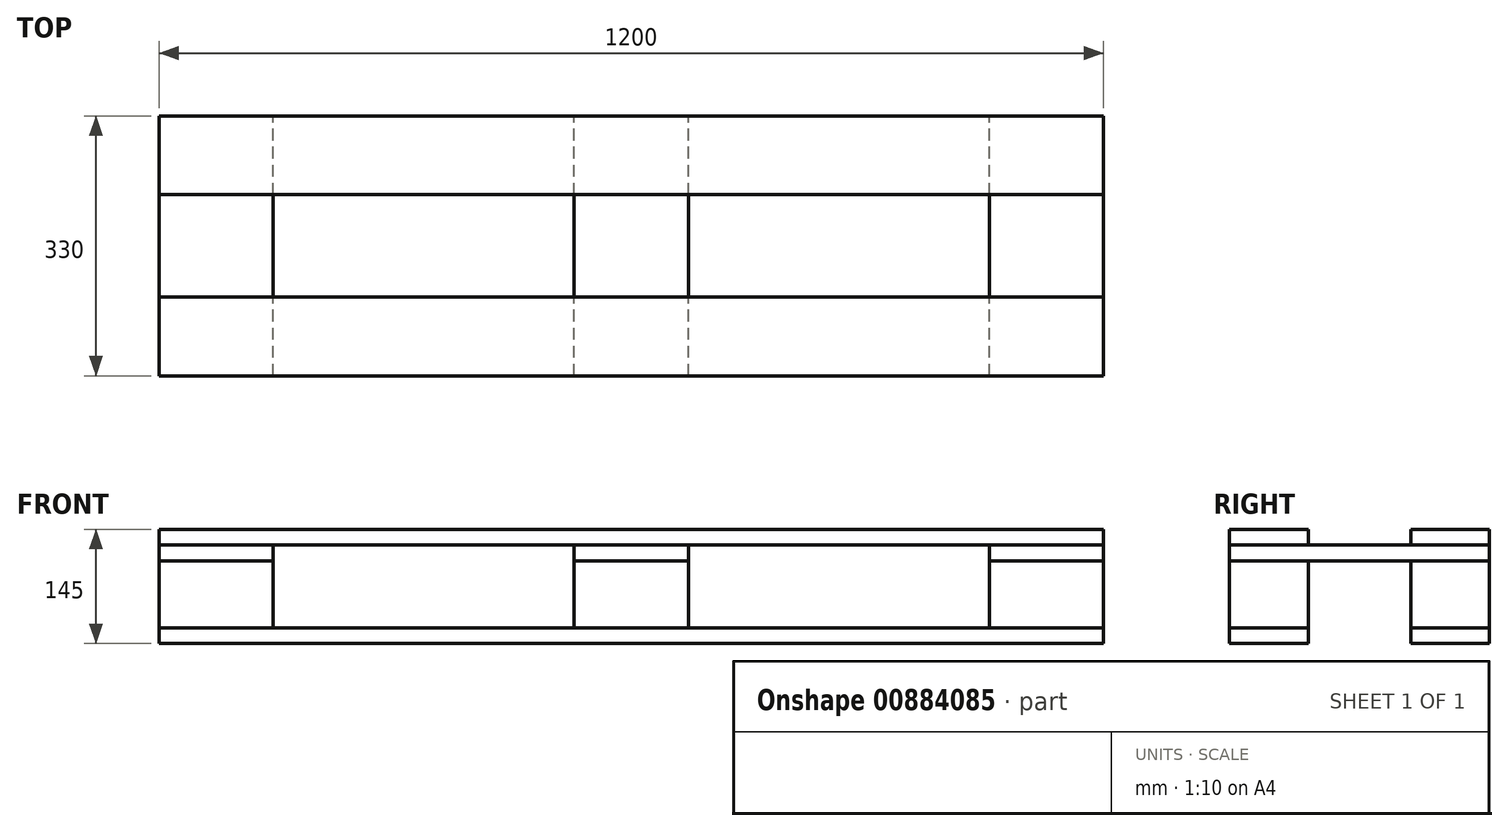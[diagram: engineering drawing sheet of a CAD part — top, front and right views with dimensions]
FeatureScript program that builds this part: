
annotation { "Feature Type Name" : "Feature", "Feature Type Description" : "" }
export const myFeature = defineFeature(function(context is Context, id is Id, definition is map)
    precondition{}
    {
        {
            var Q0;
            Q0=qCreatedBy(makeId("Top.planeOp"),FACE);
            var sketch = newSketch(context, id + "F0", { "sketchPlane" : qUnion([Q0])});
            skLineSegment(sketch, "E0.bottom", {"start": v(0, 0) * mm, "end": v(145, 0) * mm});
            skLineSegment(sketch, "E0.top", {"start": v(0, 330) * mm, "end": v(145, 330) * mm});
            skLineSegment(sketch, "E0.left", {"start": v(0, 0) * mm, "end": v(0, 330) * mm});
            skLineSegment(sketch, "E0.right", {"start": v(145, 0) * mm, "end": v(145, 330) * mm});
            skSolve(sketch);
        }
        {
            var Q0;
            Q0=makeQuery(id+"F0.imprint","IMPRINT",FACE,{"disambiguationData":[TD([[makeQuery(id+"F0.imprint","IMPRINT",EDGE,{"derivedFrom":sQuery(id+"F0.wireOp",EDGE,"E0.bottom")}),1.0]])]});
            extrude(context, id + "F1", {"entities" : qUnion([Q0]), "depth" : 20 * mm, "offsetDistance" : 25 * mm});
        }
        {
            var Q0;
            Q0=makeQuery(id+"F1.opExtrude","SWEPT_BODY",BODY,{"disambiguationData":[OSD([sQuery(id+"F0.wireOp",EDGE,"E0.bottom"),sQuery(id+"F0.wireOp",EDGE,"E0.top"),sQuery(id+"F0.wireOp",EDGE,"E0.left"),sQuery(id+"F0.wireOp",EDGE,"E0.right")])]});
            transform(context, id + "F2", {"entities" : qUnion([Q0]), "transformType" : TransformType.TRANSLATION_3D, "dx" : 0 * mm, "dy" : 0 * mm, "dz" : 0 * mm, "makeCopy" : true});
        }
        {
            var Q0;
            Q0=qCreatedBy(makeId("Top.planeOp"),FACE);
            var sketch = newSketch(context, id + "F3", { "sketchPlane" : qUnion([Q0])});
            skLineSegment(sketch, "E1.bottom", {"start": v(0, 0) * mm, "end": v(145, 0) * mm});
            skLineSegment(sketch, "E1.top", {"start": v(0, 100) * mm, "end": v(145, 100) * mm});
            skLineSegment(sketch, "E1.left", {"start": v(0, 0) * mm, "end": v(0, 100) * mm});
            skLineSegment(sketch, "E1.right", {"start": v(145, 0) * mm, "end": v(145, 100) * mm});
            skSolve(sketch);
        }
        {
            var Q0;
            Q0=makeQuery(id+"F3.imprint","IMPRINT",FACE,{"disambiguationData":[TD([[makeQuery(id+"F3.imprint","IMPRINT",EDGE,{"derivedFrom":sQuery(id+"F3.wireOp",EDGE,"E1.bottom")}),1.0]])]});
            extrude(context, id + "F4", {"entities" : qUnion([Q0]), "oppositeDirection" : true, "depth" : 85 * mm, "offsetDistance" : 25 * mm});
        }
        {
            var Q0;
            Q0=makeQuery(id+"F2.opPattern","COPY",BODY,{"derivedFrom":makeQuery(id+"F1.opExtrude","SWEPT_BODY",BODY,{"disambiguationData":[OSD([sQuery(id+"F0.wireOp",EDGE,"E0.bottom"),sQuery(id+"F0.wireOp",EDGE,"E0.top"),sQuery(id+"F0.wireOp",EDGE,"E0.left"),sQuery(id+"F0.wireOp",EDGE,"E0.right")])]}),"instanceName":"1"});
            deleteBodies(context, id + "F5", {"entities" : qUnion([Q0])});
        }
        {
            var Q0;
            Q0=makeQuery(id+"F4.opExtrude","SWEPT_BODY",BODY,{"disambiguationData":[OSD([sQuery(id+"F3.wireOp",EDGE,"E1.bottom"),sQuery(id+"F3.wireOp",EDGE,"E1.top"),sQuery(id+"F3.wireOp",EDGE,"E1.left"),sQuery(id+"F3.wireOp",EDGE,"E1.right")])]});
            transform(context, id + "F6", {"entities" : qUnion([Q0]), "transformType" : TransformType.TRANSLATION_3D, "dx" : 0 * mm, "dy" : 230 * mm, "dz" : 0 * mm, "makeCopy" : true});
        }
        {
            var Q0;
            Q0=makeQuery(id+"F1.opExtrude","CAP_FACE",FACE,{"disambiguationData":[OSD([sQuery(id+"F0.wireOp",EDGE,"E0.bottom"),sQuery(id+"F0.wireOp",EDGE,"E0.top"),sQuery(id+"F0.wireOp",EDGE,"E0.left"),sQuery(id+"F0.wireOp",EDGE,"E0.right")])],"isStart":false});
            var sketch = newSketch(context, id + "F7", { "sketchPlane" : qUnion([Q0])});
            skLineSegment(sketch, "E2.bottom", {"start": v(0, 0) * mm, "end": v(1200, 0) * mm});
            skLineSegment(sketch, "E2.top", {"start": v(0, 100) * mm, "end": v(1200, 100) * mm});
            skLineSegment(sketch, "E2.left", {"start": v(0, 0) * mm, "end": v(0, 100) * mm});
            skLineSegment(sketch, "E2.right", {"start": v(1200, 0) * mm, "end": v(1200, 100) * mm});
            skSolve(sketch);
        }
        {
            var Q0;
            {var subQ0=sQuery(id+"F7.wireOp",EDGE,"E2.left");Q0=makeQuery(id+"F7.imprint","IMPRINT",FACE,{"disambiguationData":[TD([[makeQuery(id+"F7.imprint","IMPRINT",EDGE,{"derivedFrom":subQ0}),-1.0]])]});}
            var Q1;
            {var subQ3=sQuery(id+"F7.wireOp",EDGE,"E2.right");Q1=makeQuery(id+"F7.imprint","IMPRINT",FACE,{"disambiguationData":[TD([[makeQuery(id+"F7.imprint","IMPRINT",EDGE,{"derivedFrom":subQ3}),1.0]])]});}
            extrude(context, id + "F8", {"entities" : qUnion([Q0, Q1]), "depth" : 20 * mm, "offsetDistance" : 25 * mm});
        }
        {
            var Q0;
            Q0=makeQuery(id+"F8.opExtrude","SWEPT_BODY",BODY,{"disambiguationData":[OSD([sQuery(id+"F7.wireOp",EDGE,"E2.bottom"),sQuery(id+"F7.wireOp",EDGE,"E2.top"),sQuery(id+"F7.wireOp",EDGE,"E2.left"),sQuery(id+"F7.wireOp",EDGE,"E2.right")])]});
            transform(context, id + "F9", {"entities" : qUnion([Q0]), "transformType" : TransformType.TRANSLATION_3D, "dx" : 0 * mm, "dy" : 230 * mm, "dz" : 0 * mm, "makeCopy" : true});
        }
        {
            var Q0;
            Q0=makeQuery(id+"F1.opExtrude","SWEPT_BODY",BODY,{"disambiguationData":[OSD([sQuery(id+"F0.wireOp",EDGE,"E0.bottom"),sQuery(id+"F0.wireOp",EDGE,"E0.top"),sQuery(id+"F0.wireOp",EDGE,"E0.left"),sQuery(id+"F0.wireOp",EDGE,"E0.right")])]});
            transform(context, id + "F10", {"entities" : qUnion([Q0]), "transformType" : TransformType.TRANSLATION_3D, "dx" : 1055 * mm, "dy" : 0 * mm, "dz" : 0 * mm, "makeCopy" : true});
        }
        {
            var Q0;
            Q0=makeQuery(id+"F4.opExtrude","SWEPT_BODY",BODY,{"disambiguationData":[OSD([sQuery(id+"F3.wireOp",EDGE,"E1.bottom"),sQuery(id+"F3.wireOp",EDGE,"E1.top"),sQuery(id+"F3.wireOp",EDGE,"E1.left"),sQuery(id+"F3.wireOp",EDGE,"E1.right")])]});
            var Q1;
            Q1=makeQuery(id+"F6.opPattern","COPY",BODY,{"derivedFrom":makeQuery(id+"F4.opExtrude","SWEPT_BODY",BODY,{"disambiguationData":[OSD([sQuery(id+"F3.wireOp",EDGE,"E1.bottom"),sQuery(id+"F3.wireOp",EDGE,"E1.top"),sQuery(id+"F3.wireOp",EDGE,"E1.left"),sQuery(id+"F3.wireOp",EDGE,"E1.right")])]}),"instanceName":"1"});
            transform(context, id + "F11", {"entities" : qUnion([Q0, Q1]), "transformType" : TransformType.TRANSLATION_3D, "dx" : 1055 * mm, "dy" : 0 * mm, "dz" : 0 * mm, "makeCopy" : true});
        }
        {
            var Q0;
            Q0=makeQuery(id+"F1.opExtrude","SWEPT_BODY",BODY,{"disambiguationData":[OSD([sQuery(id+"F0.wireOp",EDGE,"E0.bottom"),sQuery(id+"F0.wireOp",EDGE,"E0.top"),sQuery(id+"F0.wireOp",EDGE,"E0.left"),sQuery(id+"F0.wireOp",EDGE,"E0.right")])]});
            var Q1;
            Q1=makeQuery(id+"F4.opExtrude","SWEPT_BODY",BODY,{"disambiguationData":[OSD([sQuery(id+"F3.wireOp",EDGE,"E1.bottom"),sQuery(id+"F3.wireOp",EDGE,"E1.top"),sQuery(id+"F3.wireOp",EDGE,"E1.left"),sQuery(id+"F3.wireOp",EDGE,"E1.right")])]});
            var Q2;
            Q2=makeQuery(id+"F6.opPattern","COPY",BODY,{"derivedFrom":makeQuery(id+"F4.opExtrude","SWEPT_BODY",BODY,{"disambiguationData":[OSD([sQuery(id+"F3.wireOp",EDGE,"E1.bottom"),sQuery(id+"F3.wireOp",EDGE,"E1.top"),sQuery(id+"F3.wireOp",EDGE,"E1.left"),sQuery(id+"F3.wireOp",EDGE,"E1.right")])]}),"instanceName":"1"});
            transform(context, id + "F12", {"entities" : qUnion([Q0, Q1, Q2]), "transformType" : TransformType.TRANSLATION_3D, "dx" : 527.5 * mm, "dy" : 0 * mm, "dz" : 0 * mm, "makeCopy" : true});
        }
        {
            var Q0;
            Q0=makeQuery(id+"F8.opExtrude","SWEPT_BODY",BODY,{"disambiguationData":[OSD([sQuery(id+"F7.wireOp",EDGE,"E2.bottom"),sQuery(id+"F7.wireOp",EDGE,"E2.top"),sQuery(id+"F7.wireOp",EDGE,"E2.left"),sQuery(id+"F7.wireOp",EDGE,"E2.right")])]});
            var Q1;
            Q1=makeQuery(id+"F9.opPattern","COPY",BODY,{"derivedFrom":makeQuery(id+"F8.opExtrude","SWEPT_BODY",BODY,{"disambiguationData":[OSD([sQuery(id+"F7.wireOp",EDGE,"E2.bottom"),sQuery(id+"F7.wireOp",EDGE,"E2.top"),sQuery(id+"F7.wireOp",EDGE,"E2.left"),sQuery(id+"F7.wireOp",EDGE,"E2.right")])]}),"instanceName":"1"});
            transform(context, id + "F13", {"entities" : qUnion([Q0, Q1]), "transformType" : TransformType.TRANSLATION_3D, "dx" : 0 * mm, "dy" : 0 * mm, "dz" : -125 * mm, "makeCopy" : true});
        }
    });
